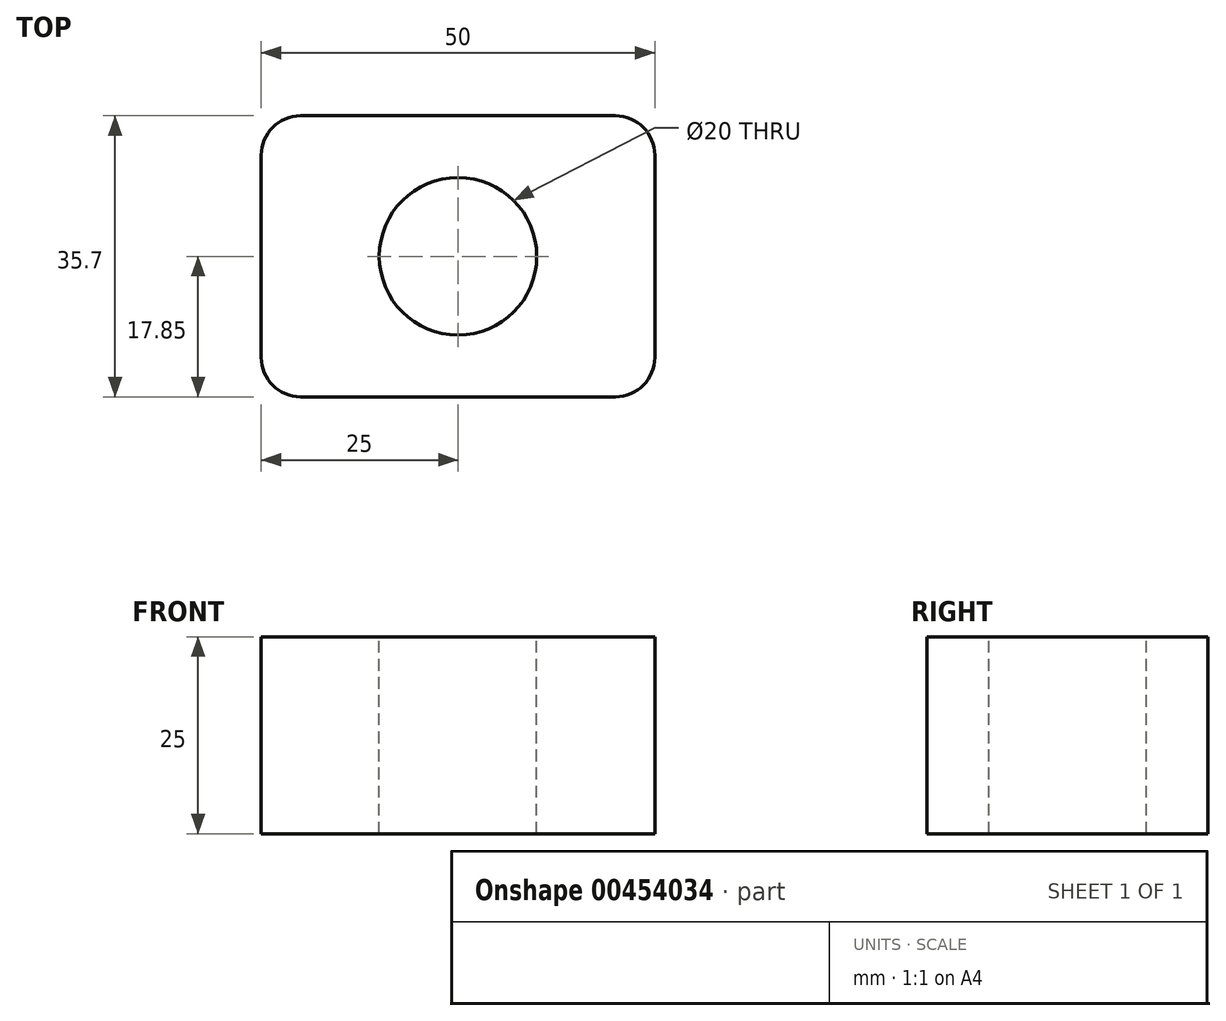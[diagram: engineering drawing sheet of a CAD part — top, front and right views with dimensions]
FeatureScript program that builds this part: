
annotation { "Feature Type Name" : "Feature", "Feature Type Description" : "" }
export const myFeature = defineFeature(function(context is Context, id is Id, definition is map)
    precondition{}
    {
        {
            var Q0;
            Q0=qCreatedBy(makeId("Top.planeOp"),FACE);
            var sketch = newSketch(context, id + "F0", { "sketchPlane" : qUnion([Q0])});
            skLineSegment(sketch, "E0.bottom", {"start": v(-25, 17.85) * mm, "end": v(25, 17.85) * mm});
            skLineSegment(sketch, "E0.top", {"start": v(-25, -17.85) * mm, "end": v(25, -17.85) * mm});
            skLineSegment(sketch, "E0.left", {"start": v(-25, 17.85) * mm, "end": v(-25, -17.85) * mm});
            skLineSegment(sketch, "E0.right", {"start": v(25, 17.85) * mm, "end": v(25, -17.85) * mm});
            skPoint(sketch, "E0.middle", {"position": v(0, 0) * mm});
            skSolve(sketch);
        }
        {
            var Q0;
            Q0=makeQuery(id+"F0.imprint","IMPRINT",FACE,{"disambiguationData":[TD([[makeQuery(id+"F0.imprint","IMPRINT",EDGE,{"derivedFrom":sQuery(id+"F0.wireOp",EDGE,"E0.bottom")}),-1.0]])]});
            extrude(context, id + "F1", {"entities" : qUnion([Q0]), "depth" : 25 * mm});
        }
        {
            var Q0;
            Q0=makeQuery(id+"F1.opExtrude","CAP_FACE",FACE,{"disambiguationData":[OSD([sQuery(id+"F0.wireOp",EDGE,"E0.bottom"),sQuery(id+"F0.wireOp",EDGE,"E0.top"),sQuery(id+"F0.wireOp",EDGE,"E0.left"),sQuery(id+"F0.wireOp",EDGE,"E0.right")])],"isStart":false});
            var sketch = newSketch(context, id + "F2", { "sketchPlane" : qUnion([Q0])});
            skCircle(sketch, "E1", {"center": v(0, 0) * mm, "radius": 10 * mm});
            skSolve(sketch);
        }
        {
            var Q0;
            Q0=makeQuery(id+"F2.imprint","IMPRINT",FACE,{"disambiguationData":[TD([[makeQuery(id+"F2.imprint","IMPRINT",EDGE,{"derivedFrom":sQuery(id+"F2.wireOp",EDGE,"E1")}),1.0]])]});
            extrude(context, id + "F3", {"entities" : qUnion([Q0]), "operationType" : NewBodyOperationType.REMOVE, "oppositeDirection" : true, "depth" : 25 * mm});
        }
        {
            var Q0;
            Q0=makeQuery(id+"F1.opExtrude","SWEPT_EDGE",EDGE,{"disambiguationData":[OSD([sQuery(id+"F0.wireOp",EDGE,"E0.bottom"),sQuery(id+"F0.wireOp",EDGE,"E0.left")])]});
            var Q1;
            Q1=makeQuery(id+"F1.opExtrude","SWEPT_EDGE",EDGE,{"disambiguationData":[OSD([sQuery(id+"F0.wireOp",EDGE,"E0.top"),sQuery(id+"F0.wireOp",EDGE,"E0.left")])]});
            var Q2;
            Q2=makeQuery(id+"F1.opExtrude","SWEPT_EDGE",EDGE,{"disambiguationData":[OSD([sQuery(id+"F0.wireOp",EDGE,"E0.top"),sQuery(id+"F0.wireOp",EDGE,"E0.right")])]});
            var Q3;
            Q3=makeQuery(id+"F1.opExtrude","SWEPT_EDGE",EDGE,{"disambiguationData":[OSD([sQuery(id+"F0.wireOp",EDGE,"E0.bottom"),sQuery(id+"F0.wireOp",EDGE,"E0.right")])]});
            fillet(context, id + "F4", {"entities" : qUnion([Q0, Q1, Q2, Q3]), "radius" : 5 * mm, "tangentPropagation" : true, "allowEdgeOverflow" : false});
        }
    });
